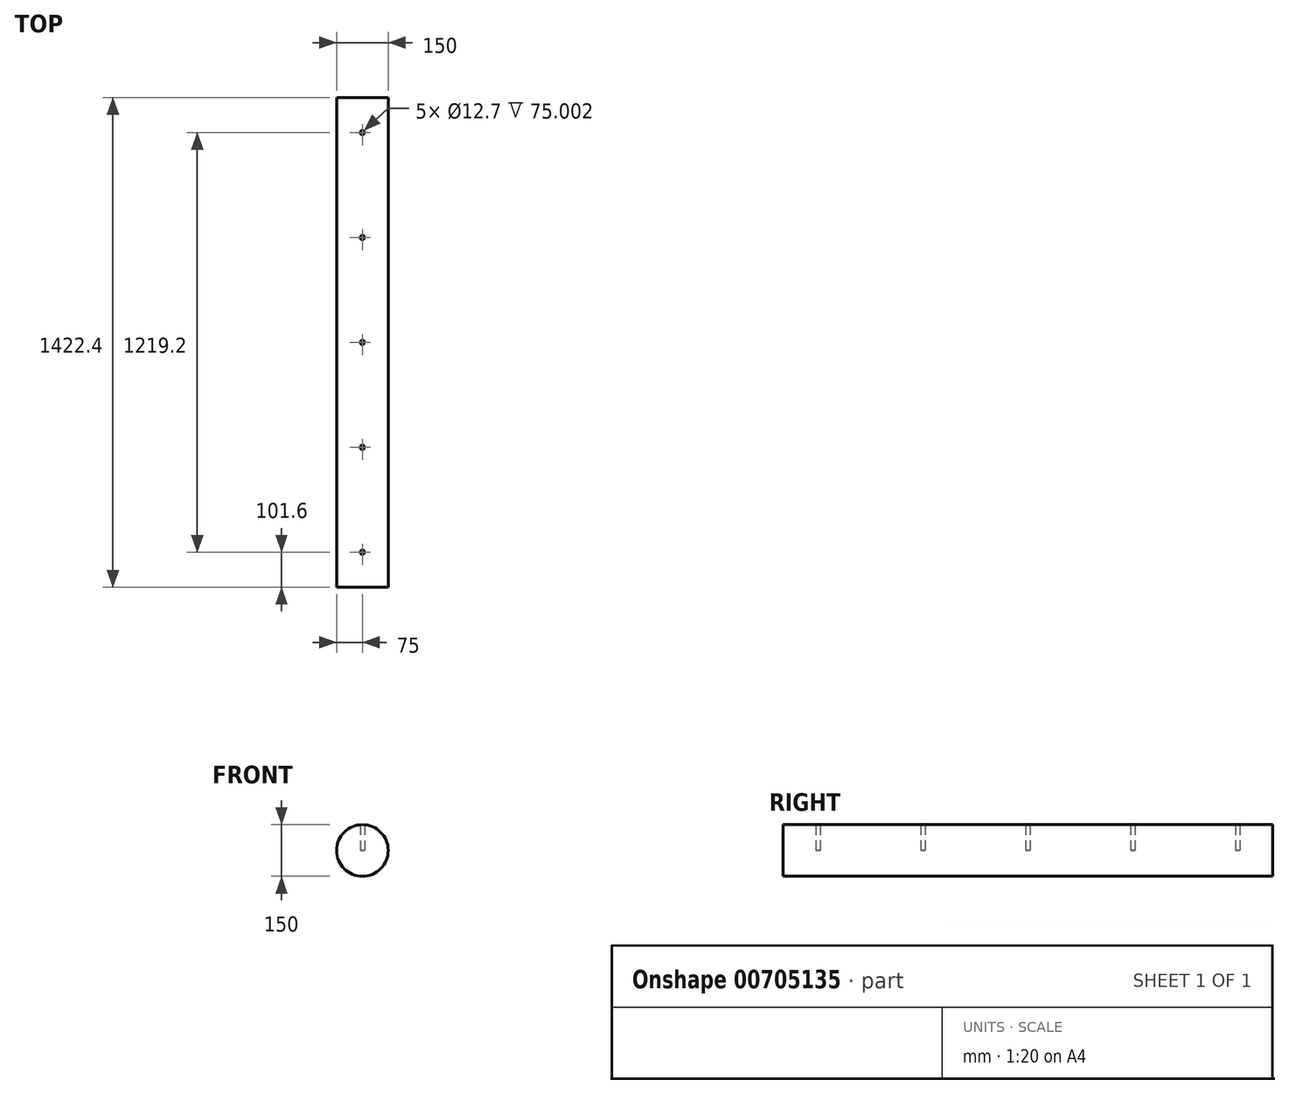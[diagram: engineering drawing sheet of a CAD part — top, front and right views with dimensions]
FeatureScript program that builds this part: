
annotation { "Feature Type Name" : "Feature", "Feature Type Description" : "" }
export const myFeature = defineFeature(function(context is Context, id is Id, definition is map)
    precondition{}
    {
        {
            var Q0;
            Q0=qCreatedBy(makeId("Front.planeOp"),FACE);
            var sketch = newSketch(context, id + "F0", { "sketchPlane" : qUnion([Q0])});
            skCircle(sketch, "E0", {"center": v(0, 0) * mm, "radius": 75 * mm});
            skSolve(sketch);
        }
        {
            var Q0;
            Q0 = qSketchRegion(id + "F0", true);
            extrude(context, id + "F1", {"entities" : qUnion([Q0]), "depth" : 1422.4 * mm, "offsetDistance" : 25.4 * mm});
        }
        {
            var Q0;
            Q0=qCreatedBy(makeId("Top.planeOp"),FACE);
            var sketch = newSketch(context, id + "F2", { "sketchPlane" : qUnion([Q0])});
            skCircle(sketch, "E1", {"center": v(0, -711.2) * mm, "radius": 6.35 * mm});
            skCircle(sketch, "E2", {"center": v(0, -406.4) * mm, "radius": 6.35 * mm});
            skCircle(sketch, "E3", {"center": v(0, -1016) * mm, "radius": 6.35 * mm});
            skCircle(sketch, "E4", {"center": v(0, -1320.8) * mm, "radius": 6.35 * mm});
            skCircle(sketch, "E5", {"center": v(0, -101.6) * mm, "radius": 6.35 * mm});
            skSolve(sketch);
        }
        {
            var Q0;
            Q0 = qSketchRegion(id + "F2", true);
            extrude(context, id + "F3", {"entities" : qUnion([Q0]), "operationType" : NewBodyOperationType.REMOVE, "depth" : 127 * mm, "offsetDistance" : 25.4 * mm});
        }
    });
